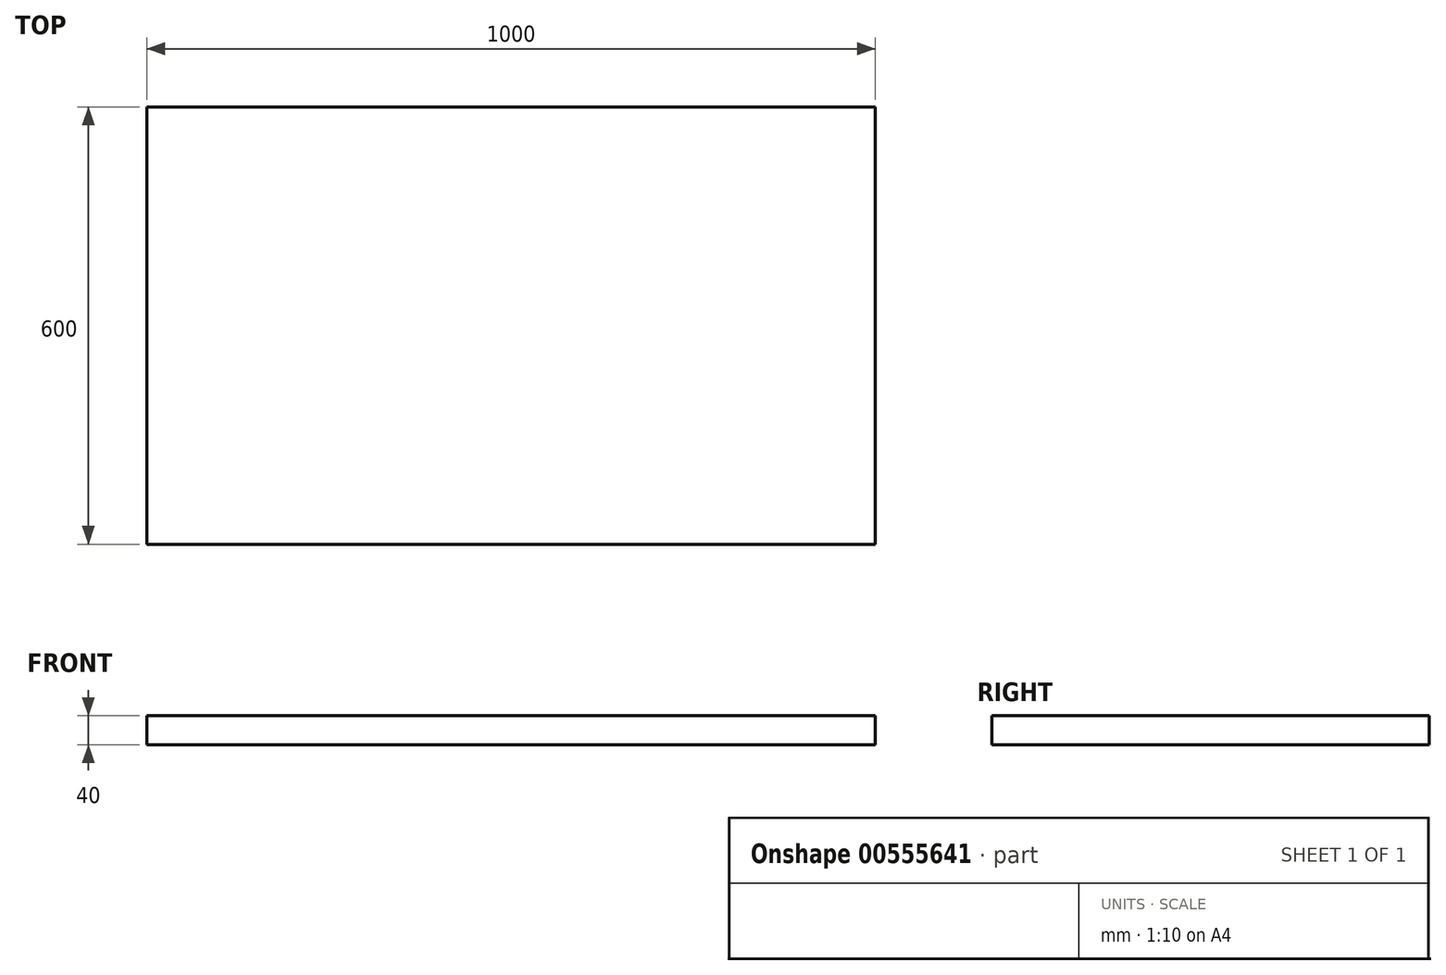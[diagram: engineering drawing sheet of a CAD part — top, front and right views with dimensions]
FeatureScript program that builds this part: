
annotation { "Feature Type Name" : "Feature", "Feature Type Description" : "" }
export const myFeature = defineFeature(function(context is Context, id is Id, definition is map)
    precondition{}
    {
        {
            var Q0;
            Q0=qCreatedBy(makeId("Top.planeOp"),FACE);
            var sketch = newSketch(context, id + "F0", { "sketchPlane" : qUnion([Q0])});
            skLineSegment(sketch, "E0.bottom", {"start": v(500, -300) * mm, "end": v(-500, -300) * mm});
            skLineSegment(sketch, "E0.top", {"start": v(500, 300) * mm, "end": v(-500, 300) * mm});
            skLineSegment(sketch, "E0.left", {"start": v(500, -300) * mm, "end": v(500, 300) * mm});
            skLineSegment(sketch, "E0.right", {"start": v(-500, -300) * mm, "end": v(-500, 300) * mm});
            skPoint(sketch, "E0.middle", {"position": v(0, 0) * mm});
            skSolve(sketch);
        }
        {
            var Q0;
            Q0 = qSketchRegion(id + "F0", true);
            extrude(context, id + "F1", {"entities" : qUnion([Q0]), "depth" : 40 * mm, "offsetDistance" : 25 * mm});
        }
    });
